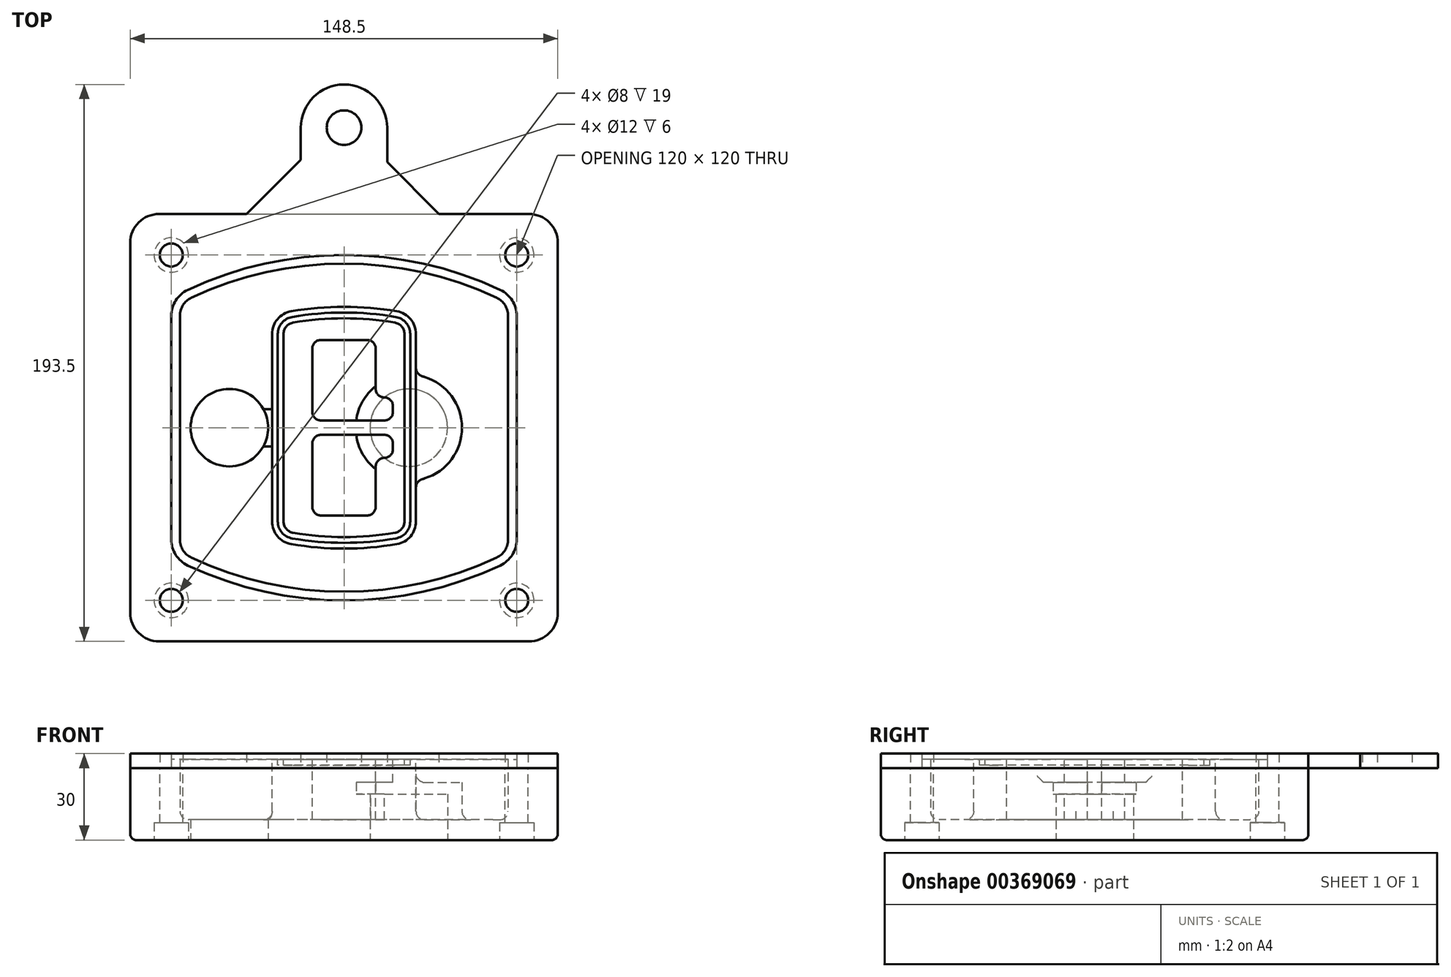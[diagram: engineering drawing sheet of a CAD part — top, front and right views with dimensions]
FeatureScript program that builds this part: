
annotation { "Feature Type Name" : "Feature", "Feature Type Description" : "" }
export const myFeature = defineFeature(function(context is Context, id is Id, definition is map)
    precondition{}
    {
        {
            var Q0;
            Q0=qCreatedBy(makeId("Top.planeOp"),FACE);
            var sketch = newSketch(context, id + "F0", { "sketchPlane" : qUnion([Q0])});
            skPoint(sketch, "E0.rect.middle", {"position": v(0, 0) * mm});
            skLineSegment(sketch, "E1.bottom", {"start": v(-64.25, -74.25) * mm, "end": v(64.25, -74.25) * mm});
            skLineSegment(sketch, "E1.top", {"start": v(-64.25, 74.25) * mm, "end": v(64.25, 74.25) * mm});
            skLineSegment(sketch, "E1.left", {"start": v(-74.25, -64.25) * mm, "end": v(-74.25, 64.25) * mm});
            skLineSegment(sketch, "E1.right", {"start": v(74.25, -64.25) * mm, "end": v(74.25, 64.25) * mm});
            skLineSegment(sketch, "E2", {"start": v(-74.25, 74.25) * mm, "end": v(74.25, -74.25) * mm, "construction": true});
            skLineSegment(sketch, "E3", {"start": v(74.25, 74.25) * mm, "end": v(-74.25, -74.25) * mm, "construction": true});
            skCircle(sketch, "E4", {"center": v(-60, 60) * mm, "radius": 4 * mm});
            skCircle(sketch, "E5", {"center": v(60, 60) * mm, "radius": 4 * mm});
            skCircle(sketch, "E6", {"center": v(60, -60) * mm, "radius": 4 * mm});
            skCircle(sketch, "E7", {"center": v(-60, -60) * mm, "radius": 4 * mm});
            skLineSegment(sketch, "E8", {"start": v(-60, 60) * mm, "end": v(60, 60) * mm, "construction": true});
            skLineSegment(sketch, "E9", {"start": v(60, 60) * mm, "end": v(60, -60) * mm, "construction": true});
            skLineSegment(sketch, "E10", {"start": v(60, -60) * mm, "end": v(-60, -60) * mm, "construction": true});
            skLineSegment(sketch, "E11", {"start": v(-60, -60) * mm, "end": v(-60, 60) * mm, "construction": true});
            skLineSegment(sketch, "E12", {"start": v(-60, 38.83) * mm, "end": v(-60, -38.83) * mm});
            skLineSegment(sketch, "E13", {"start": v(60, 38.83) * mm, "end": v(60, -38.83) * mm});
            skArc(sketch, "E14", {"start": v(54.26, 47.88) * mm, "mid": v(0, 60) * mm, "end": v(-54.26, 47.88) * mm});
            skArc(sketch, "E15", {"start": v(-54.26, -47.88) * mm, "mid": v(0, -60) * mm, "end": v(54.26, -47.88) * mm});
            skLineSegment(sketch, "E16", {"start": v(-60, 0) * mm, "end": v(60, 0) * mm, "construction": true});
            skPoint(sketch, "E17.visualSharp", {"position": v(-60, -45) * mm});
            skArc(sketch, "E17.filletArc", {"start": v(-60, -38.83) * mm, "mid": v(-58.44, -44.2) * mm, "end": v(-54.26, -47.88) * mm});
            skPoint(sketch, "E18.visualSharp", {"position": v(-60, 45) * mm});
            skArc(sketch, "E18.filletArc", {"start": v(-54.26, 47.88) * mm, "mid": v(-58.44, 44.2) * mm, "end": v(-60, 38.83) * mm});
            skPoint(sketch, "E19.visualSharp", {"position": v(60, 45) * mm});
            skArc(sketch, "E19.filletArc", {"start": v(60, 38.83) * mm, "mid": v(58.44, 44.2) * mm, "end": v(54.26, 47.88) * mm});
            skPoint(sketch, "E20.visualSharp", {"position": v(60, -45) * mm});
            skArc(sketch, "E20.filletArc", {"start": v(54.26, -47.88) * mm, "mid": v(58.44, -44.2) * mm, "end": v(60, -38.83) * mm});
            skPoint(sketch, "E21.visualSharp", {"position": v(-74.25, 74.25) * mm});
            skArc(sketch, "E21.filletArc", {"start": v(-64.25, 74.25) * mm, "mid": v(-71.32, 71.32) * mm, "end": v(-74.25, 64.25) * mm});
            skPoint(sketch, "E22.visualSharp", {"position": v(74.25, 74.25) * mm});
            skArc(sketch, "E22.filletArc", {"start": v(74.25, 64.25) * mm, "mid": v(71.32, 71.32) * mm, "end": v(64.25, 74.25) * mm});
            skPoint(sketch, "E23.visualSharp", {"position": v(74.25, -74.25) * mm});
            skArc(sketch, "E23.filletArc", {"start": v(64.25, -74.25) * mm, "mid": v(71.32, -71.32) * mm, "end": v(74.25, -64.25) * mm});
            skPoint(sketch, "E24.visualSharp", {"position": v(-74.25, -74.25) * mm});
            skArc(sketch, "E24.filletArc", {"start": v(-74.25, -64.25) * mm, "mid": v(-71.32, -71.32) * mm, "end": v(-64.25, -74.25) * mm});
            skArc(sketch, "E25.0", {"start": v(57, 38.83) * mm, "mid": v(55.9, 42.58) * mm, "end": v(52.98, 45.17) * mm});
            skLineSegment(sketch, "E25.1", {"start": v(57, 38.83) * mm, "end": v(57, -38.83) * mm});
            skArc(sketch, "E25.2", {"start": v(52.98, -45.17) * mm, "mid": v(55.9, -42.58) * mm, "end": v(57, -38.83) * mm});
            skArc(sketch, "E25.3", {"start": v(-52.98, -45.17) * mm, "mid": v(0, -57) * mm, "end": v(52.98, -45.17) * mm});
            skArc(sketch, "E25.4", {"start": v(-57, -38.83) * mm, "mid": v(-55.9, -42.58) * mm, "end": v(-52.98, -45.17) * mm});
            skArc(sketch, "E25.5", {"start": v(52.98, 45.17) * mm, "mid": v(0, 57) * mm, "end": v(-52.98, 45.17) * mm});
            skLineSegment(sketch, "E25.6", {"start": v(-57, 38.83) * mm, "end": v(-57, -38.83) * mm});
            skArc(sketch, "E25.7", {"start": v(-52.98, 45.17) * mm, "mid": v(-55.9, 42.58) * mm, "end": v(-57, 38.83) * mm});
            skArc(sketch, "E26.0", {"start": v(-55.96, 51.5) * mm, "mid": v(-61.82, 46.33) * mm, "end": v(-64, 38.83) * mm});
            skArc(sketch, "E26.1", {"start": v(55.96, 51.5) * mm, "mid": v(0, 64) * mm, "end": v(-55.96, 51.5) * mm});
            skArc(sketch, "E26.2", {"start": v(64, 38.83) * mm, "mid": v(61.82, 46.33) * mm, "end": v(55.96, 51.5) * mm});
            skLineSegment(sketch, "E26.3", {"start": v(64, 38.83) * mm, "end": v(64, -38.83) * mm});
            skArc(sketch, "E26.4", {"start": v(55.96, -51.5) * mm, "mid": v(61.82, -46.33) * mm, "end": v(64, -38.83) * mm});
            skLineSegment(sketch, "E26.5", {"start": v(-64, 38.83) * mm, "end": v(-64, -38.83) * mm});
            skArc(sketch, "E26.6", {"start": v(-55.96, -51.5) * mm, "mid": v(0, -64) * mm, "end": v(55.96, -51.5) * mm});
            skArc(sketch, "E26.7", {"start": v(-64, -38.83) * mm, "mid": v(-61.82, -46.33) * mm, "end": v(-55.96, -51.5) * mm});
            skSolve(sketch);
        }
        {
            var Q0;
            Q0=makeQuery(id+"F0.imprint","IMPRINT",FACE,{"disambiguationData":[TD([[makeQuery(id+"F0.imprint","IMPRINT",EDGE,{"derivedFrom":sQuery(id+"F0.wireOp",EDGE,"E1.bottom")}),1.0]])]});
            var Q1;
            Q1=makeQuery(id+"F0.imprint","IMPRINT",FACE,{"disambiguationData":[TD([[makeQuery(id+"F0.imprint","IMPRINT",EDGE,{"derivedFrom":sQuery(id+"F0.wireOp",EDGE,"E12")}),1.0]])]});
            var Q2;
            Q2=makeQuery(id+"F0.imprint","IMPRINT",FACE,{"disambiguationData":[TD([[makeQuery(id+"F0.imprint","IMPRINT",EDGE,{"derivedFrom":sQuery(id+"F0.wireOp",EDGE,"E25.0")}),1.0]])]});
            var Q3;
            Q3=makeQuery(id+"F0.imprint","IMPRINT",FACE,{"disambiguationData":[TD([[makeQuery(id+"F0.imprint","IMPRINT",EDGE,{"derivedFrom":sQuery(id+"F0.wireOp",EDGE,"E12")}),-1.0]])]});
            extrude(context, id + "F1", {"entities" : qUnion([Q0, Q1, Q2, Q3]), "oppositeDirection" : true, "depth" : 25 * mm});
        }
        {
            var Q0;
            Q0=makeQuery(id+"F0.imprint","IMPRINT",FACE,{"disambiguationData":[TD([[makeQuery(id+"F0.imprint","IMPRINT",EDGE,{"derivedFrom":sQuery(id+"F0.wireOp",EDGE,"E12")}),1.0]])]});
            extrude(context, id + "F2", {"entities" : qUnion([Q0]), "operationType" : NewBodyOperationType.ADD, "depth" : 3 * mm});
        }
        {
            var Q0;
            Q0=makeQuery(id+"F0.imprint","IMPRINT",FACE,{"disambiguationData":[TD([[makeQuery(id+"F0.imprint","IMPRINT",EDGE,{"derivedFrom":sQuery(id+"F0.wireOp",EDGE,"E25.0")}),1.0]])]});
            extrude(context, id + "F3", {"entities" : qUnion([Q0]), "operationType" : NewBodyOperationType.REMOVE, "oppositeDirection" : true, "depth" : 18 * mm});
        }
        {
            var Q0;
            Q0=makeQuery(id+"F2.opExtrude","CAP_FACE",FACE,{"disambiguationData":[OSD([sQuery(id+"F0.wireOp",EDGE,"E12"),sQuery(id+"F0.wireOp",EDGE,"E13"),sQuery(id+"F0.wireOp",EDGE,"E14"),sQuery(id+"F0.wireOp",EDGE,"E15"),sQuery(id+"F0.wireOp",EDGE,"E17.filletArc"),sQuery(id+"F0.wireOp",EDGE,"E18.filletArc"),sQuery(id+"F0.wireOp",EDGE,"E19.filletArc"),sQuery(id+"F0.wireOp",EDGE,"E20.filletArc"),sQuery(id+"F0.wireOp",EDGE,"E25.0"),sQuery(id+"F0.wireOp",EDGE,"E25.1"),sQuery(id+"F0.wireOp",EDGE,"E25.2"),sQuery(id+"F0.wireOp",EDGE,"E25.3"),sQuery(id+"F0.wireOp",EDGE,"E25.4"),sQuery(id+"F0.wireOp",EDGE,"E25.5"),sQuery(id+"F0.wireOp",EDGE,"E25.6"),sQuery(id+"F0.wireOp",EDGE,"E25.7")])],"isStart":false});
            var sketch = newSketch(context, id + "F4", { "sketchPlane" : qUnion([Q0])});
            skArc(sketch, "E27.0", {"start": v(-18.34, -40.45) * mm, "mid": v(0, -42) * mm, "end": v(18.34, -40.45) * mm});
            skArc(sketch, "E28.0", {"start": v(18.34, 40.45) * mm, "mid": v(0, 42) * mm, "end": v(-18.34, 40.45) * mm});
            skLineSegment(sketch, "E29", {"start": v(-25, 32.57) * mm, "end": v(-25, -32.57) * mm});
            skLineSegment(sketch, "E30", {"start": v(25, 32.57) * mm, "end": v(25, -32.57) * mm});
            skLineSegment(sketch, "E31", {"start": v(-25, 39.1) * mm, "end": v(25, 39.1) * mm, "construction": true});
            skLineSegment(sketch, "E32", {"start": v(-25, -39.1) * mm, "end": v(25, -39.1) * mm, "construction": true});
            skPoint(sketch, "E33.visualSharp", {"position": v(-25, 39.1) * mm});
            skArc(sketch, "E33.filletArc", {"start": v(-18.34, 40.45) * mm, "mid": v(-23.11, 37.73) * mm, "end": v(-25, 32.57) * mm});
            skPoint(sketch, "E34.visualSharp", {"position": v(25, 39.1) * mm});
            skArc(sketch, "E34.filletArc", {"start": v(25, 32.57) * mm, "mid": v(23.11, 37.73) * mm, "end": v(18.34, 40.45) * mm});
            skPoint(sketch, "E35.visualSharp", {"position": v(25, -39.1) * mm});
            skArc(sketch, "E35.filletArc", {"start": v(18.34, -40.45) * mm, "mid": v(23.11, -37.73) * mm, "end": v(25, -32.57) * mm});
            skPoint(sketch, "E36.visualSharp", {"position": v(-25, -39.1) * mm});
            skArc(sketch, "E36.filletArc", {"start": v(-25, -32.57) * mm, "mid": v(-23.11, -37.73) * mm, "end": v(-18.34, -40.45) * mm});
            skArc(sketch, "E37.0", {"start": v(52.98, 45.17) * mm, "mid": v(0, 57) * mm, "end": v(-52.98, 45.17) * mm});
            skArc(sketch, "E37.1", {"start": v(-52.98, 45.17) * mm, "mid": v(-55.9, 42.58) * mm, "end": v(-57, 38.83) * mm});
            skLineSegment(sketch, "E37.2", {"start": v(-57, 38.83) * mm, "end": v(-57, -38.83) * mm});
            skArc(sketch, "E37.3", {"start": v(-57, -38.83) * mm, "mid": v(-55.9, -42.58) * mm, "end": v(-52.98, -45.17) * mm});
            skArc(sketch, "E37.4", {"start": v(-52.98, -45.17) * mm, "mid": v(0, -57) * mm, "end": v(52.98, -45.17) * mm});
            skArc(sketch, "E37.5", {"start": v(52.98, -45.17) * mm, "mid": v(55.9, -42.58) * mm, "end": v(57, -38.83) * mm});
            skLineSegment(sketch, "E37.6", {"start": v(57, 38.83) * mm, "end": v(57, -38.83) * mm});
            skArc(sketch, "E37.7", {"start": v(57, 38.83) * mm, "mid": v(55.9, 42.58) * mm, "end": v(52.98, 45.17) * mm});
            skLineSegment(sketch, "E38.0", {"start": v(23, 32.57) * mm, "end": v(23, -32.57) * mm});
            skArc(sketch, "E38.1", {"start": v(18, -38.48) * mm, "mid": v(21.58, -36.44) * mm, "end": v(23, -32.57) * mm});
            skArc(sketch, "E38.2", {"start": v(-18, -38.48) * mm, "mid": v(0, -40) * mm, "end": v(18, -38.48) * mm});
            skArc(sketch, "E38.3", {"start": v(-23, -32.57) * mm, "mid": v(-21.58, -36.44) * mm, "end": v(-18, -38.48) * mm});
            skLineSegment(sketch, "E38.4", {"start": v(-23, 32.57) * mm, "end": v(-23, -32.57) * mm});
            skArc(sketch, "E38.5", {"start": v(23, 32.57) * mm, "mid": v(21.58, 36.44) * mm, "end": v(18, 38.48) * mm});
            skArc(sketch, "E38.6", {"start": v(-18, 38.48) * mm, "mid": v(-21.58, 36.44) * mm, "end": v(-23, 32.57) * mm});
            skArc(sketch, "E38.7", {"start": v(18, 38.48) * mm, "mid": v(0, 40) * mm, "end": v(-18, 38.48) * mm});
            skArc(sketch, "E39.0", {"start": v(21, 32.57) * mm, "mid": v(20.06, 35.15) * mm, "end": v(17.67, 36.5) * mm});
            skLineSegment(sketch, "E39.1", {"start": v(21, 32.57) * mm, "end": v(21, -32.57) * mm});
            skArc(sketch, "E39.2", {"start": v(17.67, -36.5) * mm, "mid": v(20.06, -35.15) * mm, "end": v(21, -32.57) * mm});
            skArc(sketch, "E39.3", {"start": v(-17.67, -36.5) * mm, "mid": v(0, -38) * mm, "end": v(17.67, -36.5) * mm});
            skArc(sketch, "E39.4", {"start": v(-21, -32.57) * mm, "mid": v(-20.06, -35.15) * mm, "end": v(-17.67, -36.5) * mm});
            skArc(sketch, "E39.5", {"start": v(17.67, 36.5) * mm, "mid": v(0, 38) * mm, "end": v(-17.67, 36.5) * mm});
            skLineSegment(sketch, "E39.6", {"start": v(-21, 32.57) * mm, "end": v(-21, -32.57) * mm});
            skArc(sketch, "E39.7", {"start": v(-17.67, 36.5) * mm, "mid": v(-20.06, 35.15) * mm, "end": v(-21, 32.57) * mm});
            skLineSegment(sketch, "E40", {"start": v(-25, 0) * mm, "end": v(25, 0) * mm, "construction": true});
            skLineSegment(sketch, "E41", {"start": v(-11, 5.5) * mm, "end": v(-11, 27.5) * mm});
            skLineSegment(sketch, "E42", {"start": v(-8, 30.5) * mm, "end": v(8, 30.5) * mm});
            skLineSegment(sketch, "E43", {"start": v(11, 27.5) * mm, "end": v(11, 13.5) * mm});
            skLineSegment(sketch, "E44", {"start": v(14, 10.5) * mm, "end": v(14, 10.5) * mm});
            skLineSegment(sketch, "E45", {"start": v(17, 7.5) * mm, "end": v(17, 5.5) * mm});
            skLineSegment(sketch, "E46", {"start": v(14, 2.5) * mm, "end": v(-8, 2.5) * mm});
            skPoint(sketch, "E47.visualSharp", {"position": v(-11, 30.5) * mm});
            skArc(sketch, "E47.filletArc", {"start": v(-8, 30.5) * mm, "mid": v(-10.12, 29.62) * mm, "end": v(-11, 27.5) * mm});
            skPoint(sketch, "E48.visualSharp", {"position": v(11, 30.5) * mm});
            skArc(sketch, "E48.filletArc", {"start": v(11, 27.5) * mm, "mid": v(10.12, 29.62) * mm, "end": v(8, 30.5) * mm});
            skPoint(sketch, "E49.visualSharp", {"position": v(11, 10.5) * mm});
            skArc(sketch, "E49.filletArc", {"start": v(11, 13.5) * mm, "mid": v(11.88, 11.38) * mm, "end": v(14, 10.5) * mm});
            skPoint(sketch, "E50.visualSharp", {"position": v(17, 10.5) * mm});
            skArc(sketch, "E50.filletArc", {"start": v(17, 7.5) * mm, "mid": v(16.12, 9.62) * mm, "end": v(14, 10.5) * mm});
            skPoint(sketch, "E51.visualSharp", {"position": v(17, 2.5) * mm});
            skArc(sketch, "E51.filletArc", {"start": v(14, 2.5) * mm, "mid": v(16.12, 3.38) * mm, "end": v(17, 5.5) * mm});
            skPoint(sketch, "E52.visualSharp", {"position": v(-11, 2.5) * mm});
            skArc(sketch, "E52.filletArc", {"start": v(-11, 5.5) * mm, "mid": v(-10.12, 3.38) * mm, "end": v(-8, 2.5) * mm});
            skLineSegment(sketch, "E53.0.MirrorCS", {"start": v(14, -2.5) * mm, "end": v(-8, -2.5) * mm});
            skArc(sketch, "E54.0.MirrorCS", {"start": v(-11, -5.5) * mm, "mid": v(-10.12, -3.38) * mm, "end": v(-8, -2.5) * mm});
            skLineSegment(sketch, "E55.0.MirrorCS", {"start": v(-11, -5.5) * mm, "end": v(-11, -27.5) * mm});
            skArc(sketch, "E56.0.MirrorCS", {"start": v(-8, -30.5) * mm, "mid": v(-10.12, -29.62) * mm, "end": v(-11, -27.5) * mm});
            skLineSegment(sketch, "E57.0.MirrorCS", {"start": v(-8, -30.5) * mm, "end": v(8, -30.5) * mm});
            skArc(sketch, "E58.0.MirrorCS", {"start": v(11, -27.5) * mm, "mid": v(10.12, -29.62) * mm, "end": v(8, -30.5) * mm});
            skLineSegment(sketch, "E59.0.MirrorCS", {"start": v(11, -27.5) * mm, "end": v(11, -13.5) * mm});
            skArc(sketch, "E60.0.MirrorCS", {"start": v(11, -13.5) * mm, "mid": v(11.88, -11.38) * mm, "end": v(14, -10.5) * mm});
            skArc(sketch, "E61.0.MirrorCS", {"start": v(17, -7.5) * mm, "mid": v(16.12, -9.62) * mm, "end": v(14, -10.5) * mm});
            skLineSegment(sketch, "E62.0.MirrorCS", {"start": v(17, -7.5) * mm, "end": v(17, -5.5) * mm});
            skArc(sketch, "E63.0.MirrorCS", {"start": v(14, -2.5) * mm, "mid": v(16.12, -3.38) * mm, "end": v(17, -5.5) * mm});
            skSolve(sketch);
        }
        {
            var Q0;
            Q0=makeQuery(id+"F4.imprint","IMPRINT",FACE,{"disambiguationData":[TD([[makeQuery(id+"F4.imprint","IMPRINT",EDGE,{"derivedFrom":sQuery(id+"F4.wireOp",EDGE,"E27.0")}),1.0]])]});
            var Q1;
            Q1=makeQuery(id+"F4.imprint","IMPRINT",FACE,{"disambiguationData":[TD([[makeQuery(id+"F4.imprint","IMPRINT",EDGE,{"derivedFrom":sQuery(id+"F4.wireOp",EDGE,"E38.0")}),-1.0]])]});
            var Q2;
            Q2=makeQuery(id+"F4.imprint","IMPRINT",FACE,{"disambiguationData":[TD([[makeQuery(id+"F4.imprint","IMPRINT",EDGE,{"derivedFrom":sQuery(id+"F4.wireOp",EDGE,"E39.0")}),1.0]])]});
            extrude(context, id + "F5", {"entities" : qUnion([Q0, Q1, Q2]), "operationType" : NewBodyOperationType.ADD, "endBound" : BoundingType.UP_TO_NEXT, "oppositeDirection" : true, "depth" : 25 * mm});
        }
        {
            var Q0;
            Q0=makeQuery(id+"F4.imprint","IMPRINT",FACE,{"disambiguationData":[TD([[makeQuery(id+"F4.imprint","IMPRINT",EDGE,{"derivedFrom":sQuery(id+"F4.wireOp",EDGE,"E38.0")}),-1.0]])]});
            extrude(context, id + "F6", {"entities" : qUnion([Q0]), "operationType" : NewBodyOperationType.REMOVE, "oppositeDirection" : true, "depth" : 2 * mm});
        }
        {
            var Q0;
            Q0=makeQuery(id+"F1.opExtrude","CAP_FACE",FACE,{"disambiguationData":[OSD([sQuery(id+"F0.wireOp",EDGE,"E1.bottom"),sQuery(id+"F0.wireOp",EDGE,"E1.top"),sQuery(id+"F0.wireOp",EDGE,"E1.left"),sQuery(id+"F0.wireOp",EDGE,"E1.right"),sQuery(id+"F0.wireOp",EDGE,"E4"),sQuery(id+"F0.wireOp",EDGE,"E5"),sQuery(id+"F0.wireOp",EDGE,"E6"),sQuery(id+"F0.wireOp",EDGE,"E7"),sQuery(id+"F0.wireOp",EDGE,"E21.filletArc"),sQuery(id+"F0.wireOp",EDGE,"E22.filletArc"),sQuery(id+"F0.wireOp",EDGE,"E23.filletArc"),sQuery(id+"F0.wireOp",EDGE,"E24.filletArc")])],"isStart":false});
            var sketch = newSketch(context, id + "F7", { "sketchPlane" : qUnion([Q0])});
            skCircle(sketch, "E64", {"center": v(22.5, 0) * mm, "radius": 13.47 * mm});
            skCircle(sketch, "E65", {"center": v(-39.81, 0) * mm, "radius": 13.47 * mm});
            skLineSegment(sketch, "E66", {"start": v(74.25, 0) * mm, "end": v(-74.25, 0) * mm});
            skCircle(sketch, "E67", {"center": v(22.5, 0) * mm, "radius": 18.47 * mm});
            skCircle(sketch, "E68", {"center": v(60, -60) * mm, "radius": 6 * mm});
            skCircle(sketch, "E69", {"center": v(-60, -60) * mm, "radius": 6 * mm});
            skCircle(sketch, "E70", {"center": v(-60, 60) * mm, "radius": 6 * mm});
            skCircle(sketch, "E71", {"center": v(60, 60) * mm, "radius": 6 * mm});
            skSolve(sketch);
        }
        {
            var Q0;
            {var subQ1=sQuery(id+"F7.wireOp",EDGE,"E66");var subQ4=sQuery(id+"F7.wireOp",EDGE,"E64");var subQ6=makeQuery(id+"F7.imprint","INTERSECT",VERTEX,{"disambiguationData":[OD(0.0)],"derivedFrom":[subQ4,subQ1]});Q0=makeQuery(id+"F7.imprint","IMPRINT",FACE,{"disambiguationData":[TD([[makeQuery(id+"F7.imprint","IMPRINT",EDGE,{"disambiguationData":[TD([[subQ6,-1.0]])],"derivedFrom":subQ4}),-1.0]])]});}
            var Q1;
            {var subQ0=sQuery(id+"F7.wireOp",EDGE,"E66");var subQ1=sQuery(id+"F7.wireOp",EDGE,"E64");var subQ3=makeQuery(id+"F7.imprint","INTERSECT",VERTEX,{"disambiguationData":[OD(0.0)],"derivedFrom":[subQ1,subQ0]});Q1=makeQuery(id+"F7.imprint","IMPRINT",FACE,{"disambiguationData":[TD([[makeQuery(id+"F7.imprint","IMPRINT",EDGE,{"disambiguationData":[TD([[subQ3,-1.0]])],"derivedFrom":subQ1}),1.0]])]});}
            var Q2;
            {var subQ0=sQuery(id+"F7.wireOp",EDGE,"E66");var subQ1=sQuery(id+"F7.wireOp",EDGE,"E64");var subQ3=makeQuery(id+"F7.imprint","INTERSECT",VERTEX,{"disambiguationData":[OD(0.0)],"derivedFrom":[subQ1,subQ0]});Q2=makeQuery(id+"F7.imprint","IMPRINT",FACE,{"disambiguationData":[TD([[makeQuery(id+"F7.imprint","IMPRINT",EDGE,{"disambiguationData":[TD([[subQ3,1.0]])],"derivedFrom":subQ1}),1.0]])]});}
            var Q3;
            {var subQ1=sQuery(id+"F7.wireOp",EDGE,"E66");var subQ4=sQuery(id+"F7.wireOp",EDGE,"E64");var subQ6=makeQuery(id+"F7.imprint","INTERSECT",VERTEX,{"disambiguationData":[OD(0.0)],"derivedFrom":[subQ4,subQ1]});Q3=makeQuery(id+"F7.imprint","IMPRINT",FACE,{"disambiguationData":[TD([[makeQuery(id+"F7.imprint","IMPRINT",EDGE,{"disambiguationData":[TD([[subQ6,1.0]])],"derivedFrom":subQ4}),-1.0]])]});}
            extrude(context, id + "F8", {"entities" : qUnion([Q0, Q1, Q2, Q3]), "operationType" : NewBodyOperationType.ADD, "oppositeDirection" : true, "depth" : 20 * mm});
        }
        {
            var Q0;
            {var subQ0=sQuery(id+"F7.wireOp",EDGE,"E66");var subQ1=sQuery(id+"F7.wireOp",EDGE,"E64");var subQ3=makeQuery(id+"F7.imprint","INTERSECT",VERTEX,{"disambiguationData":[OD(0.0)],"derivedFrom":[subQ1,subQ0]});Q0=makeQuery(id+"F7.imprint","IMPRINT",FACE,{"disambiguationData":[TD([[makeQuery(id+"F7.imprint","IMPRINT",EDGE,{"disambiguationData":[TD([[subQ3,-1.0]])],"derivedFrom":subQ1}),1.0]])]});}
            var Q1;
            {var subQ0=sQuery(id+"F7.wireOp",EDGE,"E66");var subQ1=sQuery(id+"F7.wireOp",EDGE,"E64");var subQ3=makeQuery(id+"F7.imprint","INTERSECT",VERTEX,{"disambiguationData":[OD(0.0)],"derivedFrom":[subQ1,subQ0]});Q1=makeQuery(id+"F7.imprint","IMPRINT",FACE,{"disambiguationData":[TD([[makeQuery(id+"F7.imprint","IMPRINT",EDGE,{"disambiguationData":[TD([[subQ3,1.0]])],"derivedFrom":subQ1}),1.0]])]});}
            extrude(context, id + "F9", {"entities" : qUnion([Q0, Q1]), "operationType" : NewBodyOperationType.REMOVE, "oppositeDirection" : true, "depth" : 16 * mm});
        }
        {
            var Q0;
            {var subQ0=sQuery(id+"F7.wireOp",EDGE,"E66");var subQ1=sQuery(id+"F7.wireOp",EDGE,"E65");var subQ3=makeQuery(id+"F7.imprint","INTERSECT",VERTEX,{"disambiguationData":[OD(0.0)],"derivedFrom":[subQ1,subQ0]});Q0=makeQuery(id+"F7.imprint","IMPRINT",FACE,{"disambiguationData":[TD([[makeQuery(id+"F7.imprint","IMPRINT",EDGE,{"disambiguationData":[TD([[subQ3,-1.0]])],"derivedFrom":subQ1}),1.0]])]});}
            var Q1;
            {var subQ0=sQuery(id+"F7.wireOp",EDGE,"E66");var subQ1=sQuery(id+"F7.wireOp",EDGE,"E65");var subQ3=makeQuery(id+"F7.imprint","INTERSECT",VERTEX,{"disambiguationData":[OD(0.0)],"derivedFrom":[subQ1,subQ0]});Q1=makeQuery(id+"F7.imprint","IMPRINT",FACE,{"disambiguationData":[TD([[makeQuery(id+"F7.imprint","IMPRINT",EDGE,{"disambiguationData":[TD([[subQ3,1.0]])],"derivedFrom":subQ1}),1.0]])]});}
            extrude(context, id + "F10", {"entities" : qUnion([Q0, Q1]), "operationType" : NewBodyOperationType.REMOVE, "oppositeDirection" : true, "depth" : 25 * mm});
        }
        {
            var Q0;
            Q0=makeQuery(id+"F7.imprint","IMPRINT",FACE,{"disambiguationData":[TD([[makeQuery(id+"F7.imprint","IMPRINT",EDGE,{"derivedFrom":sQuery(id+"F7.wireOp",EDGE,"E68")}),1.0]])]});
            var Q1;
            Q1=makeQuery(id+"F7.imprint","IMPRINT",FACE,{"disambiguationData":[TD([[makeQuery(id+"F7.imprint","IMPRINT",EDGE,{"derivedFrom":makeQuery(id+"F1.opExtrude","CAP_EDGE",EDGE,{"disambiguationData":[OSD([sQuery(id+"F0.wireOp",EDGE,"E5")])],"isStart":false})}),-1.0]])]});
            var Q2;
            Q2=makeQuery(id+"F7.imprint","IMPRINT",FACE,{"disambiguationData":[TD([[makeQuery(id+"F7.imprint","IMPRINT",EDGE,{"derivedFrom":sQuery(id+"F7.wireOp",EDGE,"E69")}),1.0]])]});
            var Q3;
            Q3=makeQuery(id+"F7.imprint","IMPRINT",FACE,{"disambiguationData":[TD([[makeQuery(id+"F7.imprint","IMPRINT",EDGE,{"derivedFrom":makeQuery(id+"F1.opExtrude","CAP_EDGE",EDGE,{"disambiguationData":[OSD([sQuery(id+"F0.wireOp",EDGE,"E4")])],"isStart":false})}),-1.0]])]});
            var Q4;
            Q4=makeQuery(id+"F7.imprint","IMPRINT",FACE,{"disambiguationData":[TD([[makeQuery(id+"F7.imprint","IMPRINT",EDGE,{"derivedFrom":sQuery(id+"F7.wireOp",EDGE,"E70")}),1.0]])]});
            var Q5;
            Q5=makeQuery(id+"F7.imprint","IMPRINT",FACE,{"disambiguationData":[TD([[makeQuery(id+"F7.imprint","IMPRINT",EDGE,{"derivedFrom":makeQuery(id+"F1.opExtrude","CAP_EDGE",EDGE,{"disambiguationData":[OSD([sQuery(id+"F0.wireOp",EDGE,"E7")])],"isStart":false})}),-1.0]])]});
            var Q6;
            Q6=makeQuery(id+"F7.imprint","IMPRINT",FACE,{"disambiguationData":[TD([[makeQuery(id+"F7.imprint","IMPRINT",EDGE,{"derivedFrom":sQuery(id+"F7.wireOp",EDGE,"E71")}),1.0]])]});
            var Q7;
            Q7=makeQuery(id+"F7.imprint","IMPRINT",FACE,{"disambiguationData":[TD([[makeQuery(id+"F7.imprint","IMPRINT",EDGE,{"derivedFrom":makeQuery(id+"F1.opExtrude","CAP_EDGE",EDGE,{"disambiguationData":[OSD([sQuery(id+"F0.wireOp",EDGE,"E6")])],"isStart":false})}),-1.0]])]});
            extrude(context, id + "F11", {"entities" : qUnion([Q0, Q1, Q2, Q3, Q4, Q5, Q6, Q7]), "operationType" : NewBodyOperationType.REMOVE, "oppositeDirection" : true, "depth" : 6 * mm});
        }
        {
            var Q0;
            Q0=makeQuery(id+"F9.boolean.opBoolean","COPY",FACE,{"derivedFrom":makeQuery(id+"F9.opExtrude","CAP_FACE",FACE,{"disambiguationData":[OSD([sQuery(id+"F7.wireOp",EDGE,"E64")])],"isStart":false})});
            var sketch = newSketch(context, id + "F12", { "sketchPlane" : qUnion([Q0])});
            skArc(sketch, "E72.0", {"start": v(11, 14.45) * mm, "mid": v(6.45, 9.13) * mm, "end": v(4.2, 2.5) * mm});
            skArc(sketch, "E72.1", {"start": v(4.2, -2.5) * mm, "mid": v(6.45, -9.13) * mm, "end": v(11, -14.45) * mm});
            skLineSegment(sketch, "E73", {"start": v(4.2, -2.5) * mm, "end": v(14, -2.5) * mm});
            skLineSegment(sketch, "E74.0", {"start": v(14, 2.5) * mm, "end": v(4.2, 2.5) * mm});
            skArc(sketch, "E74.1", {"start": v(14, 2.5) * mm, "mid": v(16.12, 3.38) * mm, "end": v(17, 5.5) * mm});
            skLineSegment(sketch, "E74.2", {"start": v(17, 7.5) * mm, "end": v(17, 5.5) * mm});
            skArc(sketch, "E74.3", {"start": v(17, 7.5) * mm, "mid": v(16.12, 9.62) * mm, "end": v(14, 10.5) * mm});
            skArc(sketch, "E74.4", {"start": v(11, 13.5) * mm, "mid": v(11.88, 11.38) * mm, "end": v(14, 10.5) * mm});
            skLineSegment(sketch, "E74.5", {"start": v(11, 14.45) * mm, "end": v(11, 13.5) * mm});
            skLineSegment(sketch, "E74.7", {"start": v(14, -2.5) * mm, "end": v(4.2, -2.5) * mm});
            skArc(sketch, "E74.8", {"start": v(14, -2.5) * mm, "mid": v(16.12, -3.38) * mm, "end": v(17, -5.5) * mm});
            skLineSegment(sketch, "E74.9", {"start": v(17, -7.5) * mm, "end": v(17, -5.5) * mm});
            skArc(sketch, "E74.10", {"start": v(17, -7.5) * mm, "mid": v(16.12, -9.62) * mm, "end": v(14, -10.5) * mm});
            skArc(sketch, "E74.11", {"start": v(11, -13.5) * mm, "mid": v(11.88, -11.38) * mm, "end": v(14, -10.5) * mm});
            skLineSegment(sketch, "E74.12", {"start": v(11, -14.45) * mm, "end": v(11, -13.5) * mm});
            skPoint(sketch, "E75.orphan", {"position": v(11, -27.5) * mm});
            skPoint(sketch, "E76.orphan", {"position": v(-8, -2.5) * mm});
            skPoint(sketch, "E77.orphan", {"position": v(-8, 2.5) * mm});
            skPoint(sketch, "E78.orphan", {"position": v(11, 27.5) * mm});
            skSolve(sketch);
        }
        {
            var Q0;
            {var subQ7=sQuery(id+"F12.wireOp",EDGE,"E72.0");var subQ14=sQuery(id+"F12.wireOp",EDGE,"E72.1");var subQ16=sQuery(id+"F12.wireOp",EDGE,"E74.1");var subQ18=sQuery(id+"F12.wireOp",EDGE,"E74.8");Q0=qUnion([makeQuery(id+"F12.imprint","IMPRINT",FACE,{"disambiguationData":[TD([[makeQuery(id+"F12.imprint","IMPRINT",EDGE,{"derivedFrom":subQ7}),1.0]])]}),makeQuery(id+"F12.imprint","IMPRINT",FACE,{"disambiguationData":[TD([[makeQuery(id+"F12.imprint","IMPRINT",EDGE,{"derivedFrom":subQ14}),1.0]])]}),makeQuery(id+"F12.imprint","IMPRINT",FACE,{"disambiguationData":[TD([[makeQuery(id+"F12.imprint","IMPRINT",EDGE,{"derivedFrom":subQ16}),1.0]])]}),makeQuery(id+"F12.imprint","IMPRINT",FACE,{"disambiguationData":[TD([[makeQuery(id+"F12.imprint","IMPRINT",EDGE,{"derivedFrom":subQ18}),-1.0]])]})]);}
            var Q1;
            Q1=makeQuery(id+"F5.boolean.opBoolean","SPLIT",FACE,{"disambiguationData":[TD([makeQuery(id+"F5.opExtrude","SWEPT_FACE",FACE,{"disambiguationData":[OSD([sQuery(id+"F4.wireOp",EDGE,"E41")])]})])],"derivedFrom":makeQuery(id+"F3.boolean.opBoolean","COPY",FACE,{"derivedFrom":makeQuery(id+"F3.opExtrude","CAP_FACE",FACE,{"disambiguationData":[OSD([sQuery(id+"F0.wireOp",EDGE,"E25.0"),sQuery(id+"F0.wireOp",EDGE,"E25.1"),sQuery(id+"F0.wireOp",EDGE,"E25.2"),sQuery(id+"F0.wireOp",EDGE,"E25.3"),sQuery(id+"F0.wireOp",EDGE,"E25.4"),sQuery(id+"F0.wireOp",EDGE,"E25.5"),sQuery(id+"F0.wireOp",EDGE,"E25.6"),sQuery(id+"F0.wireOp",EDGE,"E25.7")])],"isStart":false})})});
            extrude(context, id + "F13", {"entities" : qUnion([Q0]), "operationType" : NewBodyOperationType.REMOVE, "endBound" : BoundingType.UP_TO_SURFACE, "endBoundEntityFace" : qUnion([Q1]), "depth" : 25 * mm});
        }
        {
            var Q0;
            Q0=makeQuery(id+"F3.boolean.opBoolean","COPY",EDGE,{"derivedFrom":makeQuery(id+"F3.opExtrude","CAP_EDGE",EDGE,{"disambiguationData":[OSD([sQuery(id+"F0.wireOp",EDGE,"E25.6")])],"isStart":false})});
            var Q1;
            Q1=makeQuery(id+"F8.boolean.opBoolean","INTERSECT",EDGE,{"derivedFrom":[makeQuery(id+"F5.opExtrude","SWEPT_FACE",FACE,{"disambiguationData":[OSD([sQuery(id+"F4.wireOp",EDGE,"E30")])]}),makeQuery(id+"F8.opExtrude","CAP_FACE",FACE,{"disambiguationData":[OSD([sQuery(id+"F7.wireOp",EDGE,"E67")])],"isStart":false})]});
            var Q2;
            Q2=makeQuery(id+"F8.boolean.opBoolean","INTERSECT",EDGE,{"disambiguationData":[OD(1.0)],"derivedFrom":[makeQuery(id+"F5.opExtrude","SWEPT_FACE",FACE,{"disambiguationData":[OSD([sQuery(id+"F4.wireOp",EDGE,"E30")])]}),makeQuery(id+"F8.opExtrude","SWEPT_FACE",FACE,{"disambiguationData":[OSD([sQuery(id+"F7.wireOp",EDGE,"E67")])]})]});
            var Q3;
            {var subQ0=sQuery(id+"F4.wireOp",EDGE,"E30");Q3=makeQuery(id+"F8.boolean.opBoolean","SPLIT",EDGE,{"disambiguationData":[TD([makeQuery(id+"F5.opExtrude","SWEPT_FACE",FACE,{"disambiguationData":[OSD([sQuery(id+"F4.wireOp",EDGE,"E35.filletArc")])]})])],"derivedFrom":makeQuery(id+"F5.opExtrude","CAP_EDGE",EDGE,{"disambiguationData":[OSD([subQ0])],"isStart":false})});}
            var Q4;
            {var subQ0=sQuery(id+"F0.wireOp",EDGE,"E25.7");var subQ1=sQuery(id+"F0.wireOp",EDGE,"E25.1");var subQ2=sQuery(id+"F0.wireOp",EDGE,"E25.6");var subQ3=sQuery(id+"F0.wireOp",EDGE,"E25.5");var subQ4=sQuery(id+"F0.wireOp",EDGE,"E25.4");var subQ5=sQuery(id+"F0.wireOp",EDGE,"E25.0");var subQ6=sQuery(id+"F0.wireOp",EDGE,"E25.2");var subQ7=sQuery(id+"F0.wireOp",EDGE,"E25.3");Q4=makeQuery(id+"F8.boolean.opBoolean","INTERSECT",EDGE,{"derivedFrom":[makeQuery(id+"F5.boolean.opBoolean","SPLIT",FACE,{"disambiguationData":[TD([makeQuery(id+"F2.opExtrude","SWEPT_FACE",FACE,{"disambiguationData":[OSD([subQ5])]})])],"derivedFrom":makeQuery(id+"F3.boolean.opBoolean","COPY",FACE,{"derivedFrom":makeQuery(id+"F3.opExtrude","CAP_FACE",FACE,{"disambiguationData":[OSD([subQ5,subQ1,subQ6,subQ7,subQ4,subQ3,subQ2,subQ0])],"isStart":false})})}),makeQuery(id+"F8.opExtrude","SWEPT_FACE",FACE,{"disambiguationData":[OSD([sQuery(id+"F7.wireOp",EDGE,"E67")])]})]});}
            var Q5;
            Q5=makeQuery(id+"F8.boolean.opBoolean","INTERSECT",EDGE,{"disambiguationData":[OD(0.0)],"derivedFrom":[makeQuery(id+"F5.opExtrude","SWEPT_FACE",FACE,{"disambiguationData":[OSD([sQuery(id+"F4.wireOp",EDGE,"E30")])]}),makeQuery(id+"F8.opExtrude","SWEPT_FACE",FACE,{"disambiguationData":[OSD([sQuery(id+"F7.wireOp",EDGE,"E67")])]})]});
            fillet(context, id + "F14", {"entities" : qUnion([Q0, Q1, Q2, Q3, Q4, Q5]), "radius" : 3 * mm, "tangentPropagation" : true, "allowEdgeOverflow" : false});
        }
        {
            var Q0;
            Q0=makeQuery(id+"F1.opExtrude","CAP_EDGE",EDGE,{"disambiguationData":[OSD([sQuery(id+"F0.wireOp",EDGE,"E1.bottom")])],"isStart":false});
            fillet(context, id + "F15", {"entities" : qUnion([Q0]), "radius" : 2 * mm, "tangentPropagation" : true, "allowEdgeOverflow" : false});
        }
        {
            var Q0;
            {var subQ0=sQuery(id+"F0.wireOp",EDGE,"E21.filletArc");var subQ1=sQuery(id+"F0.wireOp",EDGE,"E7");var subQ2=sQuery(id+"F0.wireOp",EDGE,"E6");var subQ3=sQuery(id+"F0.wireOp",EDGE,"E5");var subQ4=sQuery(id+"F0.wireOp",EDGE,"E4");var subQ5=sQuery(id+"F0.wireOp",EDGE,"E22.filletArc");var subQ6=sQuery(id+"F0.wireOp",EDGE,"E1.bottom");var subQ7=sQuery(id+"F0.wireOp",EDGE,"E1.right");var subQ8=sQuery(id+"F0.wireOp",EDGE,"E1.top");var subQ9=sQuery(id+"F0.wireOp",EDGE,"E1.left");var subQ10=sQuery(id+"F0.wireOp",EDGE,"E23.filletArc");var subQ11=sQuery(id+"F0.wireOp",EDGE,"E24.filletArc");Q0=makeQuery(id+"F2.boolean.opBoolean","SPLIT",FACE,{"disambiguationData":[TD([makeQuery(id+"F1.opExtrude","SWEPT_FACE",FACE,{"disambiguationData":[OSD([subQ6])]})])],"derivedFrom":makeQuery(id+"F1.opExtrude","CAP_FACE",FACE,{"disambiguationData":[OSD([subQ6,subQ8,subQ9,subQ7,subQ4,subQ3,subQ2,subQ1,subQ0,subQ5,subQ10,subQ11])],"isStart":true})});}
            var sketch = newSketch(context, id + "F16", { "sketchPlane" : qUnion([Q0])});
            skLineSegment(sketch, "E79", {"start": v(0, 74.25) * mm, "end": v(0, 104.25) * mm, "construction": true});
            skPoint(sketch, "E79.endSnap0", {"position": v(0, 74.25) * mm});
            skArc(sketch, "E80", {"start": v(15, 104.25) * mm, "mid": v(0, 119.25) * mm, "end": v(-15, 104.25) * mm});
            skCircle(sketch, "E81", {"center": v(0, 104.25) * mm, "radius": 6 * mm});
            skLineSegment(sketch, "E82", {"start": v(-15, 104.25) * mm, "end": v(-15, 93.04) * mm});
            skLineSegment(sketch, "E83", {"start": v(15, 104.25) * mm, "end": v(15, 92.25) * mm});
            skLineSegment(sketch, "E84", {"start": v(-15, 93.04) * mm, "end": v(-33.79, 74.25) * mm});
            skLineSegment(sketch, "E85", {"start": v(15, 92.25) * mm, "end": v(33, 74.25) * mm});
            skLineSegment(sketch, "E86", {"start": v(-74.25, 0) * mm, "end": v(74.25, 0) * mm});
            skArc(sketch, "E87.MirrorCS", {"start": v(15, -104.25) * mm, "mid": v(0, -119.25) * mm, "end": v(-15, -104.25) * mm});
            skCircle(sketch, "E88.MirrorC", {"center": v(0, -104.25) * mm, "radius": 6 * mm});
            skLineSegment(sketch, "E89.MirrorCS", {"start": v(-15, -104.25) * mm, "end": v(-15, -93.04) * mm});
            skLineSegment(sketch, "E90.MirrorCS", {"start": v(15, -104.25) * mm, "end": v(15, -92.25) * mm});
            skLineSegment(sketch, "E91.MirrorCS", {"start": v(0, -74.25) * mm, "end": v(0, -104.25) * mm, "construction": true});
            skLineSegment(sketch, "E92.MirrorCS", {"start": v(-15, -93.04) * mm, "end": v(-33.79, -74.25) * mm});
            skPoint(sketch, "E93.MirrorP", {"position": v(0, -74.25) * mm});
            skLineSegment(sketch, "E94.MirrorCS", {"start": v(15, -92.25) * mm, "end": v(33, -74.25) * mm});
            skSolve(sketch);
        }
        {
            var Q0;
            Q0=makeQuery(id+"F16.imprint","IMPRINT",FACE,{"disambiguationData":[TD([[makeQuery(id+"F16.imprint","IMPRINT",EDGE,{"derivedFrom":sQuery(id+"F16.wireOp",EDGE,"E80")}),1.0]])]});
            var Q1;
            Q1=makeQuery(id+"F16.imprint","IMPRINT",FACE,{"disambiguationData":[TD([[makeQuery(id+"F16.imprint","IMPRINT",EDGE,{"derivedFrom":makeQuery(id+"F1.opExtrude","CAP_EDGE",EDGE,{"disambiguationData":[OSD([sQuery(id+"F0.wireOp",EDGE,"E4")])],"isStart":true})}),-1.0]])]});
            var Q2;
            Q2=makeQuery(id+"F16.imprint","IMPRINT",FACE,{"disambiguationData":[TD([[makeQuery(id+"F16.imprint","IMPRINT",EDGE,{"derivedFrom":makeQuery(id+"F1.opExtrude","CAP_EDGE",EDGE,{"disambiguationData":[OSD([sQuery(id+"F0.wireOp",EDGE,"E6")])],"isStart":true})}),-1.0]])]});
            var Q3;
            Q3=makeQuery(id+"F16.imprint","IMPRINT",FACE,{"disambiguationData":[TD([[makeQuery(id+"F16.imprint","IMPRINT",EDGE,{"derivedFrom":sQuery(id+"F16.wireOp",EDGE,"E87.MirrorCS")}),-1.0]])]});
            extrude(context, id + "F17", {"entities" : qUnion([Q0, Q1, Q2, Q3]), "depth" : 5 * mm});
        }
    });
